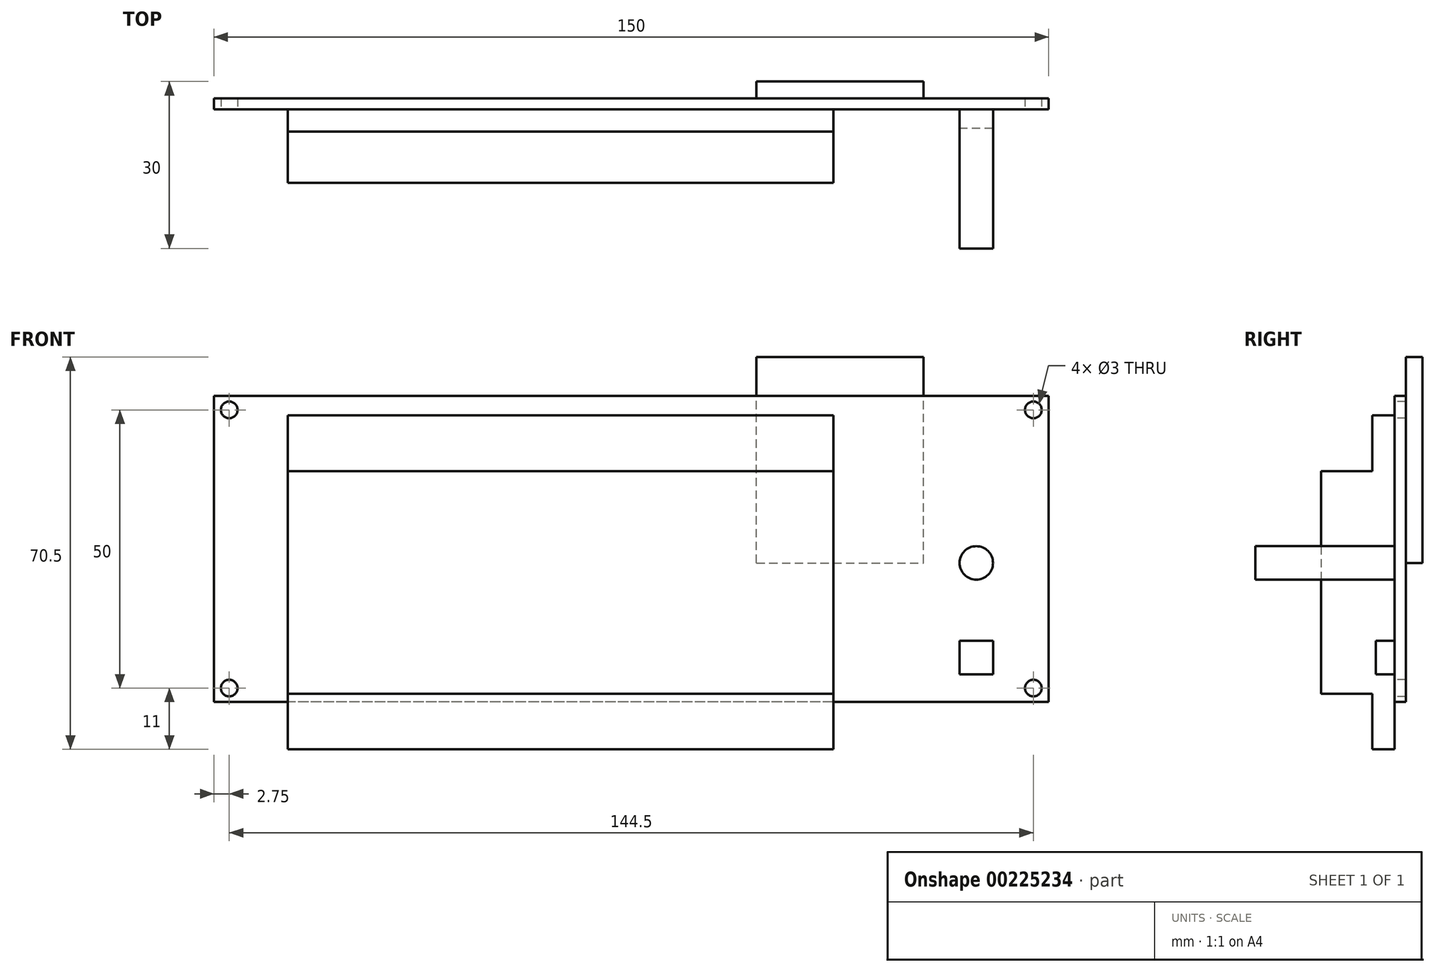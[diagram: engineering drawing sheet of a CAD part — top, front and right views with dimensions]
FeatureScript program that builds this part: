
annotation { "Feature Type Name" : "Feature", "Feature Type Description" : "" }
export const myFeature = defineFeature(function(context is Context, id is Id, definition is map)
    precondition{}
    {
        {
            var Q0;
            Q0=qCreatedBy(makeId("Front.planeOp"),FACE);
            var sketch = newSketch(context, id + "F0", { "sketchPlane" : qUnion([Q0])});
            skLineSegment(sketch, "E0.bottom", {"start": v(75, -27.5) * mm, "end": v(-75, -27.5) * mm});
            skLineSegment(sketch, "E0.top", {"start": v(75, 27.5) * mm, "end": v(-75, 27.5) * mm});
            skLineSegment(sketch, "E0.left", {"start": v(75, -27.5) * mm, "end": v(75, 27.5) * mm});
            skLineSegment(sketch, "E0.right", {"start": v(-75, -27.5) * mm, "end": v(-75, 27.5) * mm});
            skPoint(sketch, "E0.middle", {"position": v(0, 0) * mm});
            skSolve(sketch);
        }
        {
            var Q0;
            Q0 = qSketchRegion(id + "F0", true);
            extrude(context, id + "F1", {"entities" : qUnion([Q0]), "depth" : 2 * mm});
        }
        {
            var Q0;
            Q0=makeQuery(id+"F1.opExtrude","CAP_FACE",FACE,{"disambiguationData":[OSD([sQuery(id+"F0.wireOp",EDGE,"E0.bottom"),sQuery(id+"F0.wireOp",EDGE,"E0.top"),sQuery(id+"F0.wireOp",EDGE,"E0.left"),sQuery(id+"F0.wireOp",EDGE,"E0.right")])],"isStart":false});
            var sketch = newSketch(context, id + "F2", { "sketchPlane" : qUnion([Q0])});
            skCircle(sketch, "E1", {"center": v(-72.25, 25) * mm, "radius": 1.5 * mm});
            skCircle(sketch, "E2", {"center": v(-72.25, -25) * mm, "radius": 1.5 * mm});
            skCircle(sketch, "E3", {"center": v(72.25, 25) * mm, "radius": 1.5 * mm});
            skCircle(sketch, "E4", {"center": v(72.25, -25) * mm, "radius": 1.5 * mm});
            skSolve(sketch);
        }
        {
            var Q0;
            Q0 = qSketchRegion(id + "F2", true);
            extrude(context, id + "F3", {"entities" : qUnion([Q0]), "operationType" : NewBodyOperationType.REMOVE, "endBound" : BoundingType.THROUGH_ALL, "oppositeDirection" : true, "depth" : 25 * mm});
        }
        {
            var Q0;
            Q0=makeQuery(id+"F1.opExtrude","CAP_FACE",FACE,{"disambiguationData":[OSD([sQuery(id+"F0.wireOp",EDGE,"E0.bottom"),sQuery(id+"F0.wireOp",EDGE,"E0.top"),sQuery(id+"F0.wireOp",EDGE,"E0.left"),sQuery(id+"F0.wireOp",EDGE,"E0.right")])],"isStart":false});
            var sketch = newSketch(context, id + "F4", { "sketchPlane" : qUnion([Q0])});
            skCircle(sketch, "E5", {"center": v(62, -2.5) * mm, "radius": 3 * mm});
            skSolve(sketch);
        }
        {
            var Q0;
            Q0 = qSketchRegion(id + "F4", true);
            extrude(context, id + "F5", {"entities" : qUnion([Q0]), "operationType" : NewBodyOperationType.ADD, "depth" : 25 * mm});
        }
        {
            var Q0;
            Q0=makeQuery(id+"F1.opExtrude","CAP_FACE",FACE,{"disambiguationData":[OSD([sQuery(id+"F0.wireOp",EDGE,"E0.bottom"),sQuery(id+"F0.wireOp",EDGE,"E0.top"),sQuery(id+"F0.wireOp",EDGE,"E0.left"),sQuery(id+"F0.wireOp",EDGE,"E0.right")])],"isStart":false});
            var sketch = newSketch(context, id + "F6", { "sketchPlane" : qUnion([Q0])});
            skLineSegment(sketch, "E6.bottom", {"start": v(65, -22.5) * mm, "end": v(59, -22.5) * mm});
            skLineSegment(sketch, "E6.top", {"start": v(65, -16.5) * mm, "end": v(59, -16.5) * mm});
            skLineSegment(sketch, "E6.left", {"start": v(65, -22.5) * mm, "end": v(65, -16.5) * mm});
            skLineSegment(sketch, "E6.right", {"start": v(59, -22.5) * mm, "end": v(59, -16.5) * mm});
            skPoint(sketch, "E6.middle", {"position": v(62, -19.5) * mm});
            skCircle(sketch, "E7.0", {"center": v(62, -2.5) * mm, "radius": 3 * mm, "construction": true});
            skSolve(sketch);
        }
        {
            var Q0;
            Q0 = qSketchRegion(id + "F6", true);
            extrude(context, id + "F7", {"entities" : qUnion([Q0]), "operationType" : NewBodyOperationType.ADD, "depth" : 3.4 * mm});
        }
        {
            var Q0;
            Q0=makeQuery(id+"F1.opExtrude","CAP_FACE",FACE,{"disambiguationData":[OSD([sQuery(id+"F0.wireOp",EDGE,"E0.bottom"),sQuery(id+"F0.wireOp",EDGE,"E0.top"),sQuery(id+"F0.wireOp",EDGE,"E0.left"),sQuery(id+"F0.wireOp",EDGE,"E0.right")])],"isStart":false});
            var sketch = newSketch(context, id + "F8", { "sketchPlane" : qUnion([Q0])});
            skLineSegment(sketch, "E8.bottom", {"start": v(-61.7, 24) * mm, "end": v(36.3, 24) * mm});
            skLineSegment(sketch, "E8.top", {"start": v(-61.7, -36) * mm, "end": v(36.3, -36) * mm});
            skLineSegment(sketch, "E8.left", {"start": v(-61.7, 24) * mm, "end": v(-61.7, -36) * mm});
            skLineSegment(sketch, "E8.right", {"start": v(36.3, 24) * mm, "end": v(36.3, -36) * mm});
            skSolve(sketch);
        }
        {
            var Q0;
            Q0 = qSketchRegion(id + "F8", true);
            extrude(context, id + "F9", {"entities" : qUnion([Q0]), "operationType" : NewBodyOperationType.ADD, "depth" : 4 * mm});
        }
        {
            var Q0;
            Q0=makeQuery(id+"F9.opExtrude","CAP_FACE",FACE,{"disambiguationData":[OSD([sQuery(id+"F8.wireOp",EDGE,"E8.bottom"),sQuery(id+"F8.wireOp",EDGE,"E8.top"),sQuery(id+"F8.wireOp",EDGE,"E8.left"),sQuery(id+"F8.wireOp",EDGE,"E8.right")])],"isStart":false});
            var sketch = newSketch(context, id + "F10", { "sketchPlane" : qUnion([Q0])});
            skLineSegment(sketch, "E9.bottom", {"start": v(-61.7, 14) * mm, "end": v(36.3, 14) * mm});
            skLineSegment(sketch, "E9.top", {"start": v(-61.7, -26) * mm, "end": v(36.3, -26) * mm});
            skLineSegment(sketch, "E9.left", {"start": v(-61.7, 14) * mm, "end": v(-61.7, -26) * mm});
            skLineSegment(sketch, "E9.right", {"start": v(36.3, 14) * mm, "end": v(36.3, -26) * mm});
            skSolve(sketch);
        }
        {
            var Q0;
            Q0 = qSketchRegion(id + "F10", true);
            extrude(context, id + "F11", {"entities" : qUnion([Q0]), "operationType" : NewBodyOperationType.ADD, "depth" : 9.2 * mm});
        }
        {
            var Q0;
            Q0=makeQuery(id+"F1.opExtrude","CAP_FACE",FACE,{"disambiguationData":[OSD([sQuery(id+"F0.wireOp",EDGE,"E0.bottom"),sQuery(id+"F0.wireOp",EDGE,"E0.top"),sQuery(id+"F0.wireOp",EDGE,"E0.left"),sQuery(id+"F0.wireOp",EDGE,"E0.right")])],"isStart":true});
            var sketch = newSketch(context, id + "F12", { "sketchPlane" : qUnion([Q0])});
            skLineSegment(sketch, "E10.bottom", {"start": v(-22.49, -2.5) * mm, "end": v(-52.49, -2.5) * mm});
            skLineSegment(sketch, "E10.top", {"start": v(-22.49, 34.5) * mm, "end": v(-52.49, 34.5) * mm});
            skLineSegment(sketch, "E10.left", {"start": v(-22.49, -2.5) * mm, "end": v(-22.49, 34.5) * mm});
            skLineSegment(sketch, "E10.right", {"start": v(-52.49, -2.5) * mm, "end": v(-52.49, 34.5) * mm});
            skSolve(sketch);
        }
        {
            var Q0;
            Q0 = qSketchRegion(id + "F12", true);
            extrude(context, id + "F13", {"entities" : qUnion([Q0]), "operationType" : NewBodyOperationType.ADD, "depth" : 3 * mm});
        }
    });
